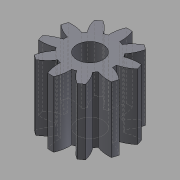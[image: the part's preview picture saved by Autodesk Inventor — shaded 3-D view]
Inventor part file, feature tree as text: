
AUTODESK INVENTOR PART (.ipt)
format: ipt  version: 2015 (Build 190159000, 159)  size: 164,864 bytes
history: native  units: in
note: dims shown in document units (in); Inventor stores cm internally (conversion verified against a paired STEP export)
features: other x13, sketch x3, plane x2
ambient origin geometry x8: Origin, YZ Plane, XZ Plane, XY Plane, X Axis, Y Axis, Z Axis, Center Point
bodies: Solid1 (feature_tree)
feature tree (18):
  other  "Spur Gear1"
  other  "Solid1::Spur Gear1"
  other  "TaggingFeature1"
  sketch  "Sketch1"  dims[d0=0.3937in]
  sketch  "Sketch2"  dims[d16=0.4724in d17=0.0in d41=0.0in d43=0.4724in d46=0.4724in d47=0.0in d48=0.0in]
  sketch  "Sketch3"
  plane  "XZ Plane_1"
  plane  "Work Plane2"
  other  "Z Axis_1"
  other  "Srf1"
  other  "Srf1::Derived"
  other  "Distance iMate"
  other  "Align iMate"
  other  "Mesh iMate"
  other  "Axis iMate"
  other  "Position iMate"
  other  "Mesh iMate2"
  other  "Start plane iMate"
